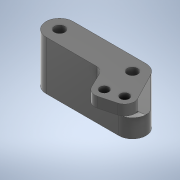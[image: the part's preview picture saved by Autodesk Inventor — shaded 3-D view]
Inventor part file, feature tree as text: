
AUTODESK INVENTOR PART (.ipt)
format: ipt  version: 2020 (Build 240168000, 168)  size: 686,592 bytes
history: native  units: mm
features: extrude x3, sketch x3, chamfer x2
ambient origin geometry x8: Origin, YZ Plane, XZ Plane, XY Plane, X Axis, Y Axis, Z Axis, Center Point
bodies: Volumenkörper1 (feature_tree)
feature tree (8):
  extrude  "Extrusion1"  Depth=5.0mm
  extrude  "Extrusion2"  Depth=23.5mm TaperAngle=0.0deg
  chamfer  "Fase1"  Distance=4.2mm
  extrude  "Extrusion3"  Depth=2.5mm
  chamfer  "Fase2"  Distance=11.0mm
  sketch  "Skizze1"  dims[d0=35.0mm d1=5.0mm]
  sketch  "Skizze2"  dims[d2=13.0mm d3=23.5mm d4=0.0mm]
  sketch  "Skizze3"  dims[d5=8.0mm d6=4.2mm d11=2.5mm d12=11.0mm d13=5.0mm d14=0.0mm d15=9.75mm d16=2.0mm d17=45.0deg d19=7.0mm d20=5.0mm d21=0.0mm d22=2.626001mm d23=14.0mm d25=8.5mm d27=0.5mm d28=2.0mm d29=45.0deg]
